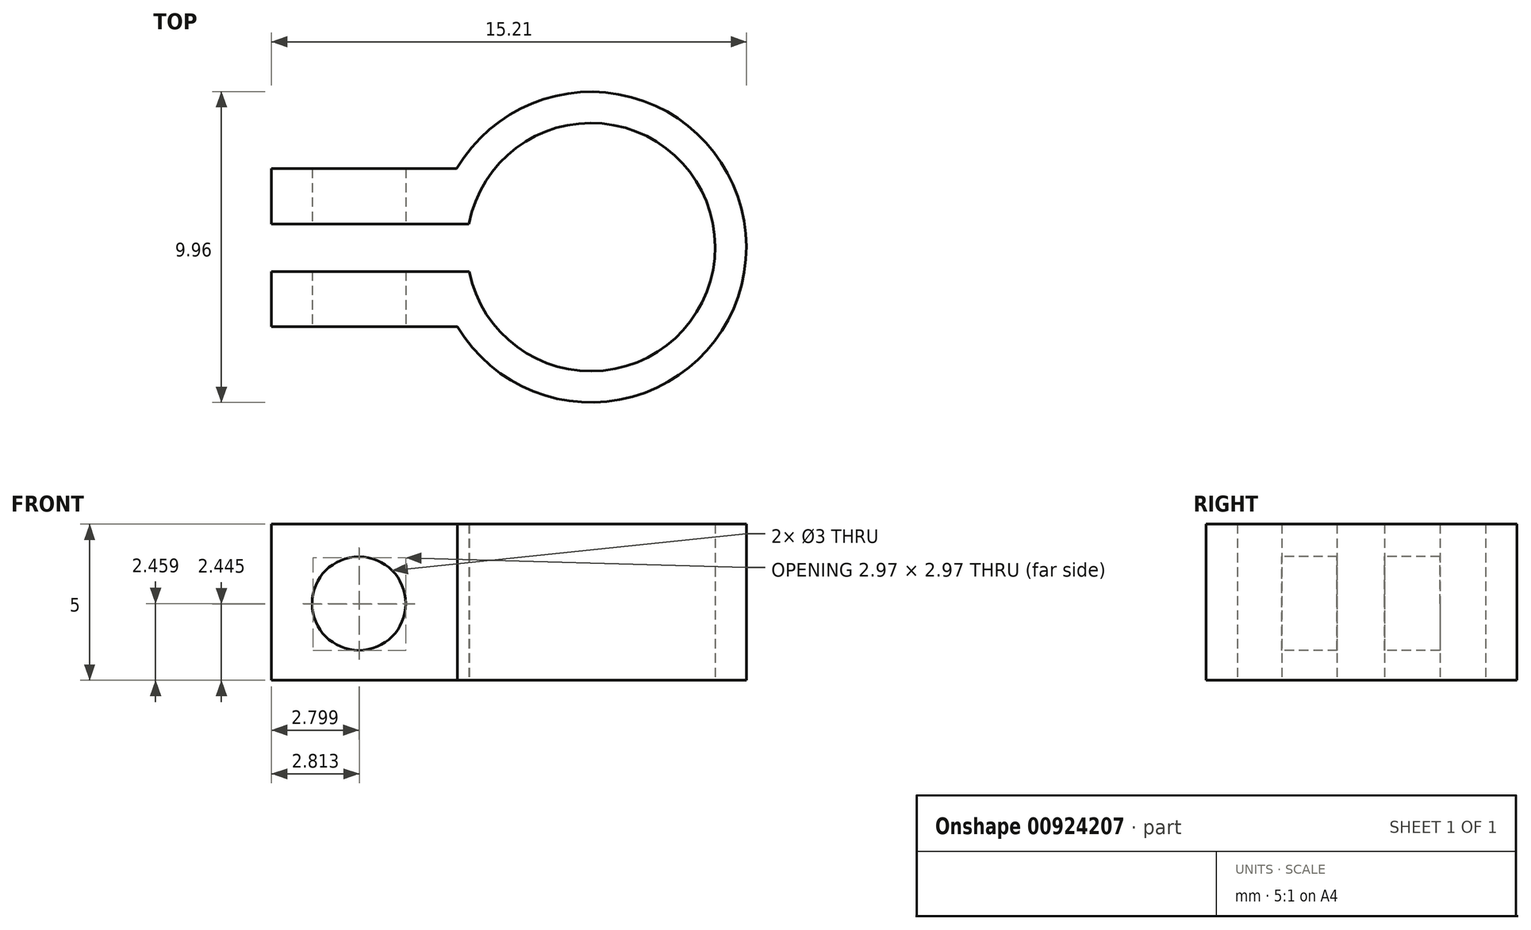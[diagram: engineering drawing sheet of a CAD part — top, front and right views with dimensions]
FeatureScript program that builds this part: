
annotation { "Feature Type Name" : "Feature", "Feature Type Description" : "" }
export const myFeature = defineFeature(function(context is Context, id is Id, definition is map)
    precondition{}
    {
        {
            var Q0;
            Q0=qCreatedBy(makeId("Top.planeOp"),FACE);
            var sketch = newSketch(context, id + "F0", { "sketchPlane" : qUnion([Q0])});
            skCircle(sketch, "E0", {"center": v(0, 0) * mm, "radius": 3.65 * mm});
            skCircle(sketch, "E1", {"center": v(0, 0) * mm, "radius": 3.98 * mm});
            skCircle(sketch, "E2", {"center": v(0, 0) * mm, "radius": 4.98 * mm});
            skLineSegment(sketch, "E3.bottom", {"start": v(-3.78, 0.74) * mm, "end": v(-10.23, 0.74) * mm});
            skLineSegment(sketch, "E3.top", {"start": v(-3.78, -0.78) * mm, "end": v(-10.23, -0.78) * mm});
            skLineSegment(sketch, "E3.left", {"start": v(-3.78, 0.74) * mm, "end": v(-3.78, -0.78) * mm});
            skLineSegment(sketch, "E3.right", {"start": v(-10.23, 0.74) * mm, "end": v(-10.23, -0.78) * mm});
            skLineSegment(sketch, "E4", {"start": v(-10.23, 0.74) * mm, "end": v(-10.23, 2.51) * mm});
            skLineSegment(sketch, "E5", {"start": v(-10.23, 2.51) * mm, "end": v(-4.3, 2.51) * mm});
            skLineSegment(sketch, "E6", {"start": v(-10.23, -0.78) * mm, "end": v(-10.23, -2.55) * mm});
            skLineSegment(sketch, "E7", {"start": v(-10.23, -2.55) * mm, "end": v(-4.28, -2.55) * mm});
            skSolve(sketch);
        }
        {
            var Q0;
            {var subQ4=sQuery(id+"F0.wireOp",EDGE,"E4");Q0=makeQuery(id+"F0.imprint","IMPRINT",FACE,{"disambiguationData":[TD([[makeQuery(id+"F0.imprint","IMPRINT",EDGE,{"derivedFrom":subQ4}),-1.0]])]});}
            var Q1;
            {var subQ4=sQuery(id+"F0.wireOp",EDGE,"E6");Q1=makeQuery(id+"F0.imprint","IMPRINT",FACE,{"disambiguationData":[TD([[makeQuery(id+"F0.imprint","IMPRINT",EDGE,{"derivedFrom":subQ4}),1.0]])]});}
            var Q2;
            {var subQ5=sQuery(id+"F0.wireOp",EDGE,"E3.bottom");var subQ7=sQuery(id+"F0.wireOp",EDGE,"E1");var subQ8=makeQuery(id+"F0.imprint","INTERSECT",VERTEX,{"derivedFrom":[subQ7,subQ5]});Q2=makeQuery(id+"F0.imprint","IMPRINT",FACE,{"disambiguationData":[TD([[makeQuery(id+"F0.imprint","IMPRINT",EDGE,{"disambiguationData":[TD([[subQ8,1.0]])],"derivedFrom":subQ7}),-1.0]])]});}
            extrude(context, id + "F1", {"entities" : qUnion([Q0, Q1, Q2]), "depth" : 5 * mm, "offsetDistance" : 25.4 * mm});
        }
        {
            var Q0;
            Q0=makeQuery(id+"F1.opExtrude","SWEPT_FACE",FACE,{"disambiguationData":[OSD([sQuery(id+"F0.wireOp",EDGE,"E7")])]});
            var sketch = newSketch(context, id + "F2", { "sketchPlane" : qUnion([Q0])});
            skCircle(sketch, "E8", {"center": v(-7.43, 2.46) * mm, "radius": 1.5 * mm});
            skSolve(sketch);
        }
        {
            var Q0;
            Q0=makeQuery(id+"F2.imprint","IMPRINT",FACE,{"disambiguationData":[TD([[makeQuery(id+"F2.imprint","IMPRINT",EDGE,{"derivedFrom":sQuery(id+"F2.wireOp",EDGE,"E8")}),1.0]])]});
            extrude(context, id + "F3", {"entities" : qUnion([Q0]), "operationType" : NewBodyOperationType.REMOVE, "oppositeDirection" : true, "depth" : 25.4 * mm, "offsetDistance" : 25.4 * mm});
        }
    });
